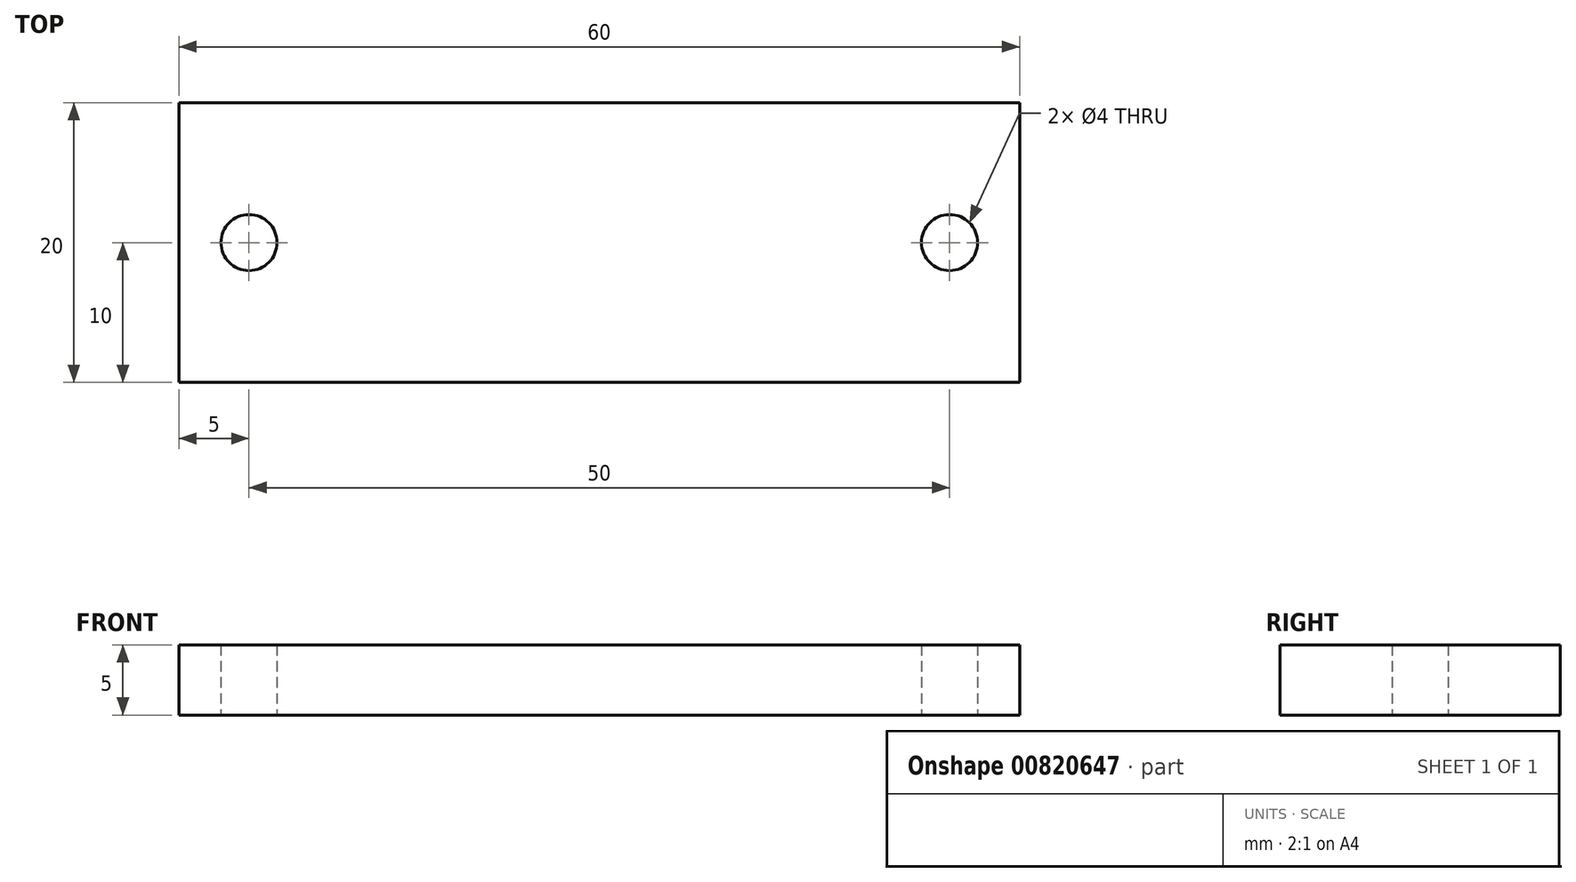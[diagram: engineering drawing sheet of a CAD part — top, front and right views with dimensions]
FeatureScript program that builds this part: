
annotation { "Feature Type Name" : "Feature", "Feature Type Description" : "" }
export const myFeature = defineFeature(function(context is Context, id is Id, definition is map)
    precondition{}
    {
        {
            var Q0;
            Q0=qCreatedBy(makeId("Top.planeOp"),FACE);
            var sketch = newSketch(context, id + "F0", { "sketchPlane" : qUnion([Q0])});
            skLineSegment(sketch, "E0.bottom", {"start": v(-30, 10) * mm, "end": v(30, 10) * mm});
            skLineSegment(sketch, "E0.top", {"start": v(-30, -10) * mm, "end": v(30, -10) * mm});
            skLineSegment(sketch, "E0.left", {"start": v(-30, 10) * mm, "end": v(-30, -10) * mm});
            skLineSegment(sketch, "E0.right", {"start": v(30, 10) * mm, "end": v(30, -10) * mm});
            skCircle(sketch, "E1", {"center": v(-25, 0) * mm, "radius": 2 * mm});
            skCircle(sketch, "E2", {"center": v(25, 0) * mm, "radius": 2 * mm});
            skSolve(sketch);
        }
        {
            var Q0;
            Q0 = qSketchRegion(id + "F0", true);
            extrude(context, id + "F1", {"entities" : qUnion([Q0]), "depth" : 5 * mm, "offsetDistance" : 25 * mm});
        }
    });
